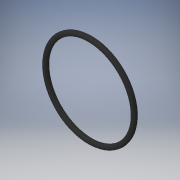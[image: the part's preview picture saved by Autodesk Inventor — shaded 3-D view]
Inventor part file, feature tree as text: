
AUTODESK INVENTOR PART (.ipt)
format: ipt  version: 2018 (Build 220112000, 112)  size: 125,440 bytes
history: native  units: in
note: dims shown in document units (in); Inventor stores cm internally (conversion verified against a paired STEP export)
features: revolve x1
ambient origin geometry x8: Origin, YZ Plane, XZ Plane, XY Plane, X Axis, Y Axis, Z Axis, Center Point
bodies: Solid1 (feature_tree)
feature tree (1):
  revolve  "Revolve1"  [1 undecoded]
note: 1 required parameter value undecoded (feature->parameter linkage not recoverable at this tier; creation-order binding heuristic only, values carry confidence <= 0.55)
